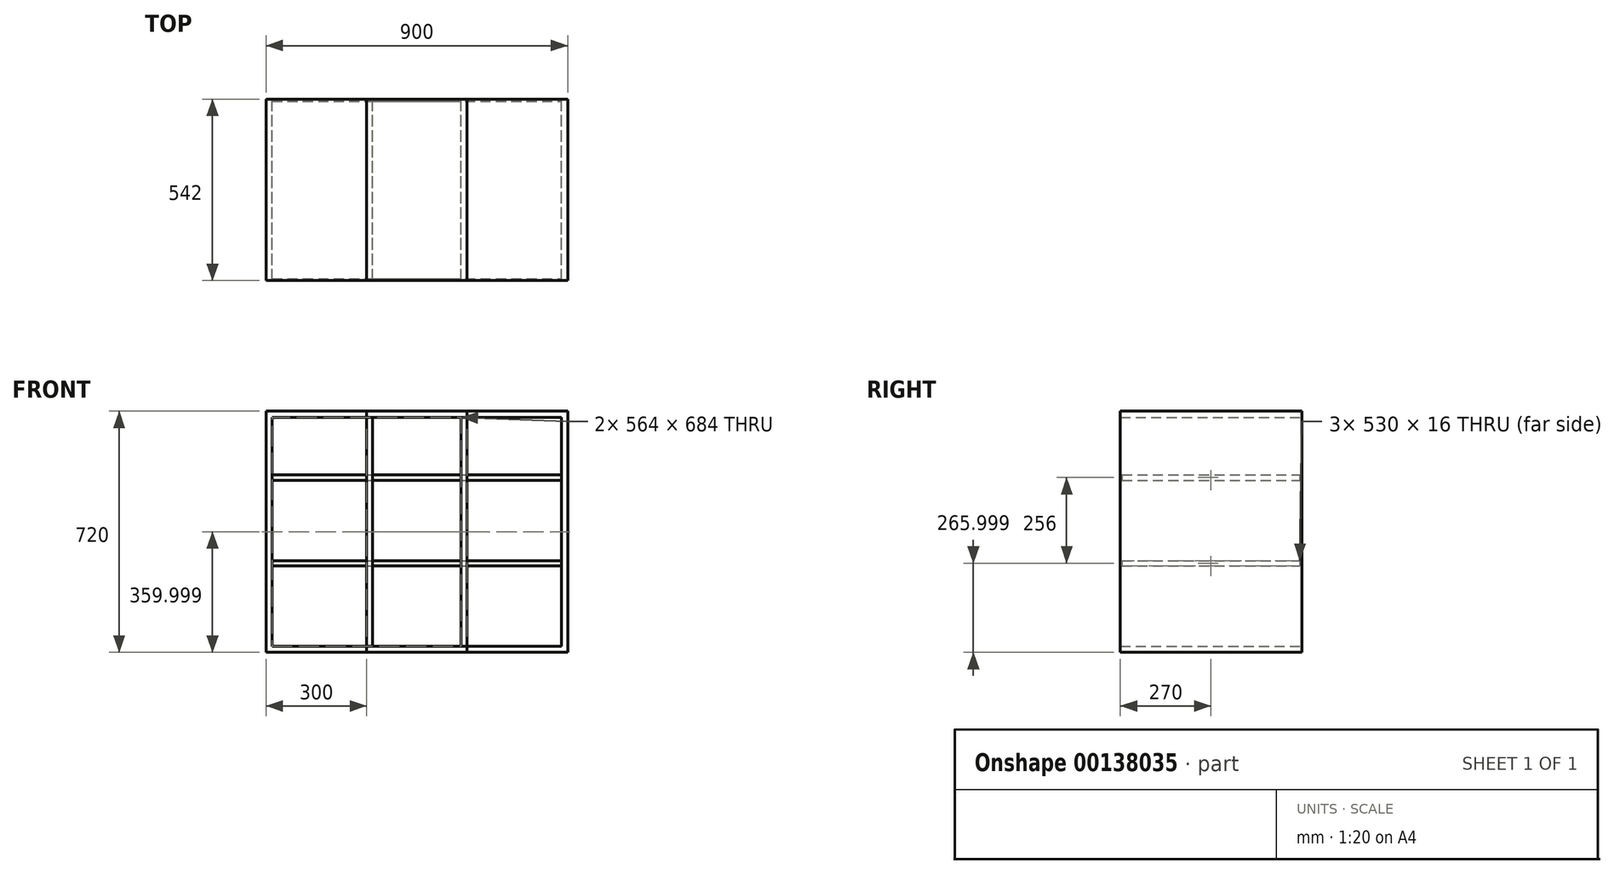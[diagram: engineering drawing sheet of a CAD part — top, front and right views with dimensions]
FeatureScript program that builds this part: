
annotation { "Feature Type Name" : "Feature", "Feature Type Description" : "" }
export const myFeature = defineFeature(function(context is Context, id is Id, definition is map)
    precondition{}
    {
        {
            var Q0;
            Q0=qCreatedBy(makeId("Front.planeOp"),FACE);
            var sketch = newSketch(context, id + "F0", { "sketchPlane" : qUnion([Q0])});
            skLineSegment(sketch, "E0", {"start": v(1126.63, -554.31) * mm, "end": v(1726.63, -554.31) * mm});
            skLineSegment(sketch, "E1", {"start": v(1726.63, -554.31) * mm, "end": v(1726.63, -1274.31) * mm});
            skLineSegment(sketch, "E2", {"start": v(1144.63, -572.31) * mm, "end": v(1708.63, -572.31) * mm});
            skLineSegment(sketch, "E3", {"start": v(1708.63, -572.31) * mm, "end": v(1708.63, -1256.31) * mm});
            skLineSegment(sketch, "E4", {"start": v(1144.63, -572.31) * mm, "end": v(1144.63, -1256.31) * mm});
            skLineSegment(sketch, "E5", {"start": v(1144.63, -1256.31) * mm, "end": v(1708.63, -1256.31) * mm});
            skLineSegment(sketch, "E6", {"start": v(1126.63, -554.31) * mm, "end": v(1126.63, -1274.31) * mm});
            skLineSegment(sketch, "E7", {"start": v(1726.63, -1274.31) * mm, "end": v(1126.63, -1274.31) * mm});
            skLineSegment(sketch, "E8", {"start": v(1144.63, -572.31) * mm, "end": v(1144.63, -744.31) * mm});
            skLineSegment(sketch, "E9", {"start": v(1144.63, -744.31) * mm, "end": v(1708.63, -744.31) * mm});
            skLineSegment(sketch, "E10", {"start": v(1708.63, -744.31) * mm, "end": v(1708.63, -572.31) * mm});
            skLineSegment(sketch, "E11", {"start": v(1144.63, -744.31) * mm, "end": v(1144.63, -760.31) * mm});
            skLineSegment(sketch, "E12", {"start": v(1144.63, -760.31) * mm, "end": v(1708.63, -760.31) * mm});
            skLineSegment(sketch, "E13", {"start": v(1144.63, -1016.31) * mm, "end": v(1707.98, -1016.31) * mm});
            skLineSegment(sketch, "E14", {"start": v(1144.63, -1000.31) * mm, "end": v(1707.98, -1000.31) * mm});
            skLineSegment(sketch, "E15", {"start": v(1708.63, -744.31) * mm, "end": v(1708.63, -760.31) * mm});
            skLineSegment(sketch, "E16", {"start": v(1707.98, -1000.31) * mm, "end": v(1707.98, -1016.31) * mm});
            skLineSegment(sketch, "E17", {"start": v(1708.63, -760.31) * mm, "end": v(1708.63, -744.31) * mm});
            skSolve(sketch);
        }
        {
            var Q0;
            Q0=makeQuery(id+"F0.imprint","IMPRINT",FACE,{"disambiguationData":[TD([[makeQuery(id+"F0.imprint","IMPRINT",EDGE,{"derivedFrom":sQuery(id+"F0.wireOp",EDGE,"E0")}),-1.0]])]});
            extrude(context, id + "F1", {"entities" : qUnion([Q0]), "depth" : 535 * mm, "hasSecondDirection" : true, "secondDirectionOppositeDirection" : true, "secondDirectionDepth" : 7 * mm});
        }
        {
            var Q0;
            Q0=makeQuery(id+"F0.imprint","IMPRINT",FACE,{"disambiguationData":[TD([[makeQuery(id+"F0.imprint","IMPRINT",EDGE,{"derivedFrom":sQuery(id+"F0.wireOp",EDGE,"E12")}),1.0]])]});
            var Q1;
            {var subQ0=sQuery(id+"F0.wireOp",EDGE,"E13");Q1=makeQuery(id+"F0.imprint","IMPRINT",FACE,{"disambiguationData":[TD([[makeQuery(id+"F0.imprint","IMPRINT",EDGE,{"derivedFrom":subQ0}),1.0]])]});}
            extrude(context, id + "F2", {"entities" : qUnion([Q0, Q1]), "operationType" : NewBodyOperationType.ADD, "depth" : 530 * mm});
        }
        {
            var Q0;
            Q0=makeQuery(id+"F1.opExtrude","SWEPT_BODY",BODY,{"disambiguationData":[OSD([sQuery(id+"F0.wireOp",EDGE,"E0"),sQuery(id+"F0.wireOp",EDGE,"E1"),sQuery(id+"F0.wireOp",EDGE,"E2"),sQuery(id+"F0.wireOp",EDGE,"E3"),sQuery(id+"F0.wireOp",EDGE,"E4"),sQuery(id+"F0.wireOp",EDGE,"E5"),sQuery(id+"F0.wireOp",EDGE,"E6"),sQuery(id+"F0.wireOp",EDGE,"E7"),sQuery(id+"F0.wireOp",EDGE,"E8"),sQuery(id+"F0.wireOp",EDGE,"E10"),sQuery(id+"F0.wireOp",EDGE,"E11"),sQuery(id+"F0.wireOp",EDGE,"E17")])]});
            transform(context, id + "F3", {"entities" : qUnion([Q0]), "transformType" : TransformType.TRANSLATION_3D, "dx" : 300 * mm, "dy" : 0 * mm, "dz" : 0 * mm, "makeCopy" : true});
        }
    });
